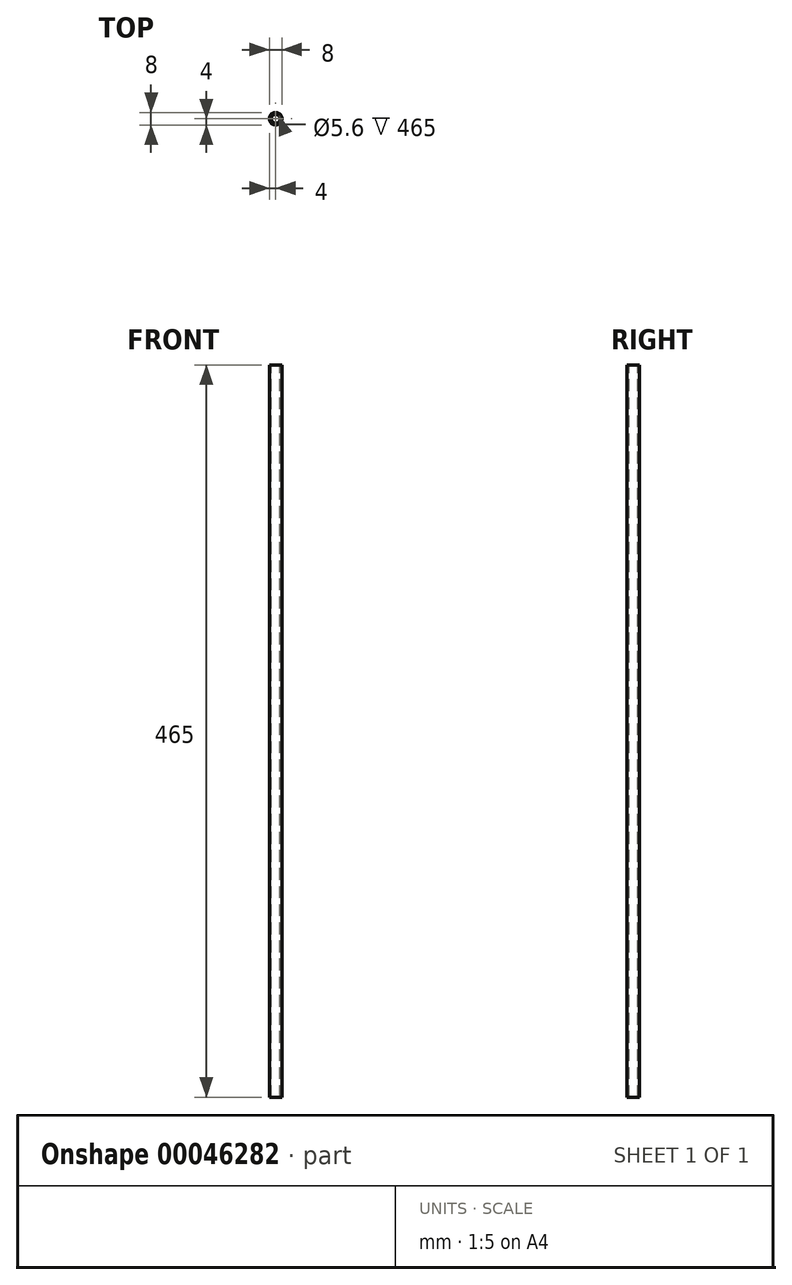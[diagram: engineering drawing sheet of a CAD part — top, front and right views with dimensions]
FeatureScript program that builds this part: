
annotation { "Feature Type Name" : "Feature", "Feature Type Description" : "" }
export const myFeature = defineFeature(function(context is Context, id is Id, definition is map)
    precondition{}
    {
        {
            var Q0;
            Q0=qCreatedBy(makeId("Top.planeOp"),FACE);
            var sketch = newSketch(context, id + "F0", { "sketchPlane" : qUnion([Q0])});
            skCircle(sketch, "E0", {"center": v(0, 0) * mm, "radius": 4 * mm});
            skCircle(sketch, "E1", {"center": v(0, 0) * mm, "radius": 2.8 * mm});
            skSolve(sketch);
        }
        {
            var Q0;
            Q0=makeQuery(id+"F0.imprint","IMPRINT",FACE,{"disambiguationData":[TD([[makeQuery(id+"F0.imprint","IMPRINT",EDGE,{"derivedFrom":sQuery(id+"F0.wireOp",EDGE,"E0")}),1.0]])]});
            extrude(context, id + "F1", {"entities" : qUnion([Q0]), "oppositeDirection" : true, "depth" : 465 * mm});
        }
    });
